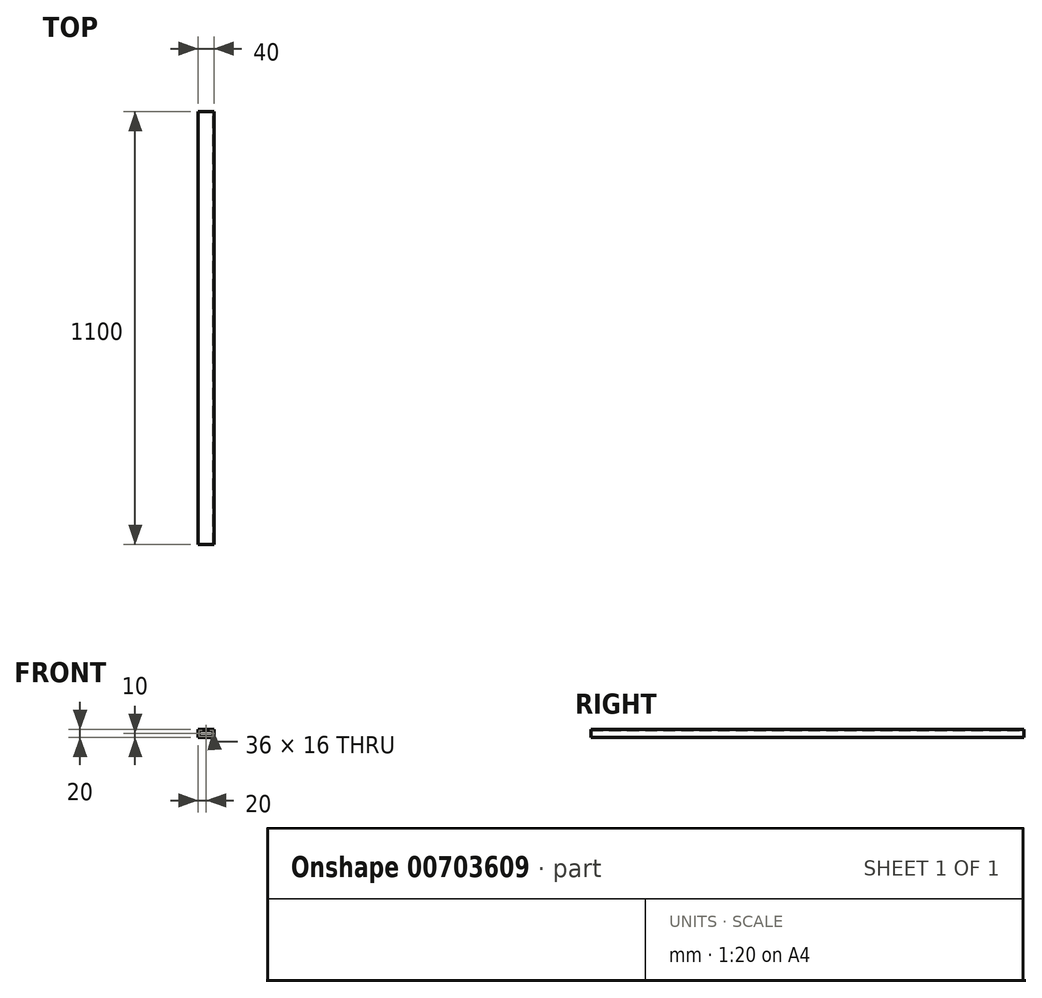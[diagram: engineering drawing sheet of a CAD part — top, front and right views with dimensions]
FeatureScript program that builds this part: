
annotation { "Feature Type Name" : "Feature", "Feature Type Description" : "" }
export const myFeature = defineFeature(function(context is Context, id is Id, definition is map)
    precondition{}
    {
        {
            var Q0;
            Q0=qCreatedBy(makeId("Front.planeOp"),FACE);
            var sketch = newSketch(context, id + "F0", { "sketchPlane" : qUnion([Q0])});
            skLineSegment(sketch, "E0.bottom", {"start": v(-20, 10) * mm, "end": v(20, 10) * mm});
            skLineSegment(sketch, "E0.top", {"start": v(-20, -10) * mm, "end": v(20, -10) * mm});
            skLineSegment(sketch, "E0.left", {"start": v(-20, 10) * mm, "end": v(-20, -10) * mm});
            skLineSegment(sketch, "E0.right", {"start": v(20, 10) * mm, "end": v(20, -10) * mm});
            skPoint(sketch, "E0.middle", {"position": v(0, 0) * mm});
            skLineSegment(sketch, "E1.bottom", {"start": v(-18, 8) * mm, "end": v(18, 8) * mm});
            skLineSegment(sketch, "E1.top", {"start": v(-18, -8) * mm, "end": v(18, -8) * mm});
            skLineSegment(sketch, "E1.left", {"start": v(-18, 8) * mm, "end": v(-18, -8) * mm});
            skLineSegment(sketch, "E1.right", {"start": v(18, 8) * mm, "end": v(18, -8) * mm});
            skSolve(sketch);
        }
        {
            var Q0;
            Q0=makeQuery(id+"F0.imprint","IMPRINT",FACE,{"disambiguationData":[TD([[makeQuery(id+"F0.imprint","IMPRINT",EDGE,{"derivedFrom":sQuery(id+"F0.wireOp",EDGE,"E0.bottom")}),-1.0]])]});
            extrude(context, id + "F1", {"entities" : qUnion([Q0]), "depth" : 1100 * mm, "offsetDistance" : 25 * mm});
        }
    });
